# Revit family: Zumtobel SUPERSYSTEM Outdoor Pole
name_source: partatom
category: Lighting Fixtures
revit_build: Autodesk Revit 2016 (Build: 20150220_1215(x64)
units: mm (PartAtom-declared; Revit-internal decimal feet)

## family parameters
Always vertical = Yes
Cut with Voids When Loaded = No
Light Source = No
OmniClass Number = 23.80.70.00
OmniClass Title = Lighting
Part Type = Normal
Room Calculation Point = No
Round Connector Dimension = Use Diameter
Shared = No
Work Plane-Based = No

## types (4) — shared parameters
Description = SUPERSYSTEM Outdoor Pole
Manufacturer = Zumtobel Lighting
Pole = Zumtobel_Metal_Black
URL = http://www.zumtobel.com

## per-type parameters (varying)
| type | Base Plate | Model | Pole Height | Underground Part |
| FO POLE 4,5M ST Q100/Q60 CHMM MGS SUS CL | No | 24162588 | 4500 mm | Yes |
| FO POLE 4,5M ST Q100/Q60 CHMM MPL SUS CL | Yes | 24162589 | 4500 mm | No |
| FO POLE 6M ST Q100/Q60 CHMM MGS SUS CL | No | 24162590 | 6000 mm  [stored 19.685 ft] | Yes |
| FO POLE 6M ST Q100/Q60 CHMM MPL SUS CL | Yes | 24162591 | 6000 mm  [stored 19.685 ft] | No |

note: [stored X ft] marks values corroborated as IEEE doubles in the binary element streams (Revit-internal decimal feet)

## geometry (parser evidence)
native form markers: Sweep x3
no freeform markers — native parametric forms only
